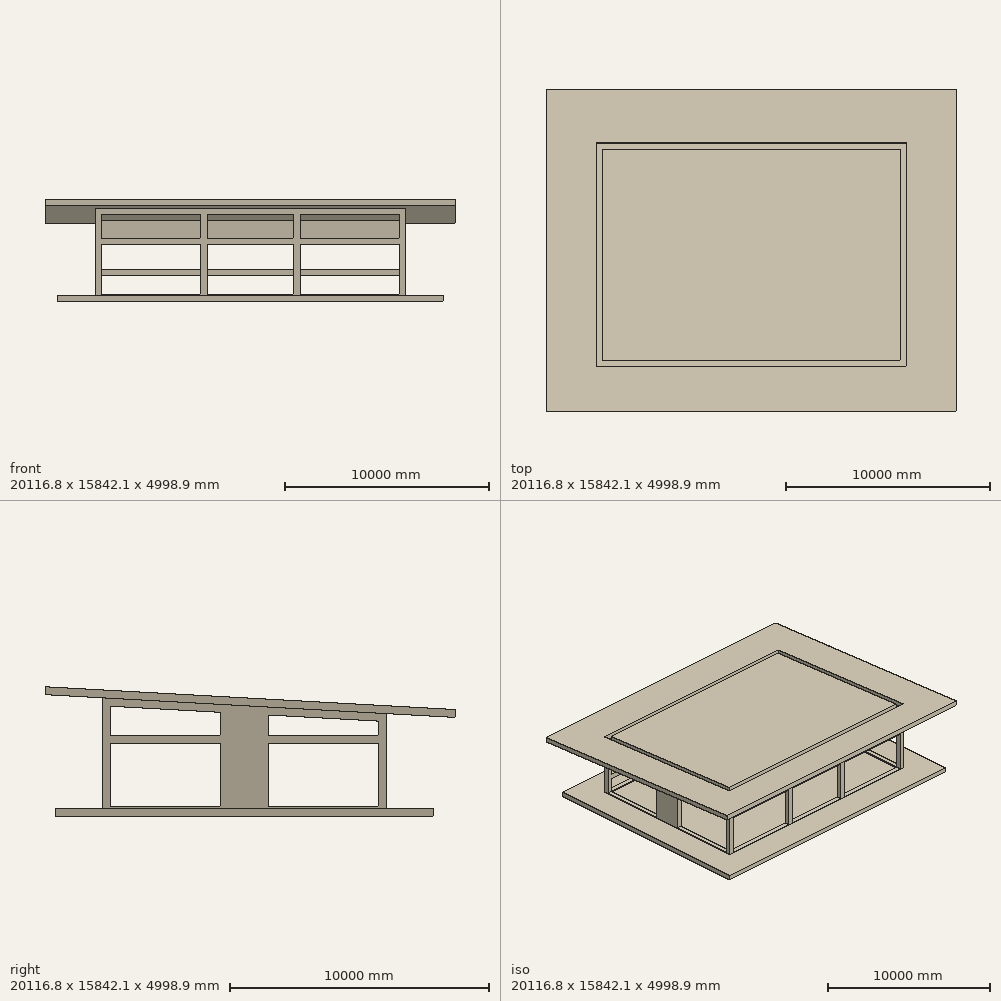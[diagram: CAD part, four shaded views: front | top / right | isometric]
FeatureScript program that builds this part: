
annotation { "Feature Type Name" : "Feature", "Feature Type Description" : "" }
export const myFeature = defineFeature(function(context is Context, id is Id, definition is map)
    precondition{}
    {
        {
            var Q0;
            Q0=qCreatedBy(makeId("Top.planeOp"),FACE);
            var sketch = newSketch(context, id + "F0", { "sketchPlane" : qUnion([Q0])});
            skLineSegment(sketch, "E0.bottom", {"start": v(9448.8, 7315.2) * mm, "end": v(-9448.8, 7315.2) * mm});
            skLineSegment(sketch, "E0.top", {"start": v(9448.8, -7315.2) * mm, "end": v(-9448.8, -7315.2) * mm});
            skLineSegment(sketch, "E0.left", {"start": v(9448.8, 7315.2) * mm, "end": v(9448.8, -7315.2) * mm});
            skLineSegment(sketch, "E0.right", {"start": v(-9448.8, 7315.2) * mm, "end": v(-9448.8, -7315.2) * mm});
            skPoint(sketch, "E0.middle", {"position": v(0, 0) * mm});
            skSolve(sketch);
        }
        {
            var Q0;
            Q0=makeQuery(id+"F0.imprint","IMPRINT",FACE,{"disambiguationData":[TD([[makeQuery(id+"F0.imprint","IMPRINT",EDGE,{"derivedFrom":sQuery(id+"F0.wireOp",EDGE,"E0.bottom")}),1.0]])]});
            extrude(context, id + "F1", {"entities" : qUnion([Q0]), "oppositeDirection" : true, "depth" : 304.8 * mm, "offsetDistance" : 30.48 * mm});
        }
        {
            var Q0;
            Q0=makeQuery(id+"F1.opExtrude","CAP_FACE",FACE,{"disambiguationData":[OSD([sQuery(id+"F0.wireOp",EDGE,"E0.bottom"),sQuery(id+"F0.wireOp",EDGE,"E0.top"),sQuery(id+"F0.wireOp",EDGE,"E0.left"),sQuery(id+"F0.wireOp",EDGE,"E0.right")])],"isStart":true});
            var sketch = newSketch(context, id + "F2", { "sketchPlane" : qUnion([Q0])});
            skLineSegment(sketch, "E1.bottom", {"start": v(7620, 5486.4) * mm, "end": v(-7620, 5486.4) * mm});
            skLineSegment(sketch, "E1.top", {"start": v(7620, -5486.4) * mm, "end": v(-7620, -5486.4) * mm});
            skLineSegment(sketch, "E1.left", {"start": v(7620, 5486.4) * mm, "end": v(7620, -5486.4) * mm});
            skLineSegment(sketch, "E1.right", {"start": v(-7620, 5486.4) * mm, "end": v(-7620, -5486.4) * mm});
            skPoint(sketch, "E1.middle", {"position": v(0, 0) * mm});
            skSolve(sketch);
        }
        {
            var Q0;
            Q0=makeQuery(id+"F2.imprint","IMPRINT",FACE,{"disambiguationData":[TD([[makeQuery(id+"F2.imprint","IMPRINT",EDGE,{"derivedFrom":sQuery(id+"F2.wireOp",EDGE,"E1.bottom")}),1.0]])]});
            extrude(context, id + "F3", {"entities" : qUnion([Q0]), "depth" : 4267.2 * mm, "offsetDistance" : 30.48 * mm});
        }
        {
            var Q0;
            Q0=makeQuery(id+"F3.opExtrude","SWEPT_FACE",FACE,{"disambiguationData":[OSD([sQuery(id+"F2.wireOp",EDGE,"E1.right")])]});
            var sketch = newSketch(context, id + "F4", { "sketchPlane" : qUnion([Q0])});
            skLineSegment(sketch, "E2", {"start": v(-5486.4, 3657.6) * mm, "end": v(5486.4, 4267.2) * mm});
            skSolve(sketch);
        }
        {
            var Q0;
            {var subQ0=sQuery(id+"F4.wireOp",EDGE,"E2");Q0=makeQuery(id+"F4.imprint","IMPRINT",FACE,{"disambiguationData":[TD([[makeQuery(id+"F4.imprint","IMPRINT",EDGE,{"derivedFrom":subQ0}),1.0]])]});}
            var Q1;
            Q1=makeQuery(id+"F3.opExtrude","SWEPT_FACE",FACE,{"disambiguationData":[OSD([sQuery(id+"F2.wireOp",EDGE,"E1.left")])]});
            extrude(context, id + "F5", {"entities" : qUnion([Q0]), "operationType" : NewBodyOperationType.REMOVE, "endBound" : BoundingType.UP_TO_SURFACE, "oppositeDirection" : true, "depth" : 10928.62 * mm, "endBoundEntityFace" : qUnion([Q1]), "offsetDistance" : 30.48 * mm});
        }
        {
            var Q0;
            Q0=makeQuery(id+"F5.boolean.opBoolean","COPY",FACE,{"derivedFrom":makeQuery(id+"F5.opExtrude","SWEPT_FACE",FACE,{"disambiguationData":[OSD([sQuery(id+"F4.wireOp",EDGE,"E2")])]})});
            var Q1;
            Q1=makeQuery(id+"F3.opExtrude","CAP_FACE",FACE,{"disambiguationData":[OSD([sQuery(id+"F2.wireOp",EDGE,"E1.bottom"),sQuery(id+"F2.wireOp",EDGE,"E1.top"),sQuery(id+"F2.wireOp",EDGE,"E1.left"),sQuery(id+"F2.wireOp",EDGE,"E1.right")])],"isStart":true});
            shell(context, id + "F6", {"entities" : qUnion([Q0, Q1]), "thickness" : 304.8 * mm});
        }
        {
            var Q0;
            Q0=makeQuery(id+"F5.boolean.opBoolean","COPY",FACE,{"derivedFrom":makeQuery(id+"F5.opExtrude","SWEPT_FACE",FACE,{"disambiguationData":[OSD([sQuery(id+"F4.wireOp",EDGE,"E2")])]})});
            var sketch = newSketch(context, id + "F7", { "sketchPlane" : qUnion([Q0])});
            skLineSegment(sketch, "E3.bottom", {"start": v(-10058.4, -7924.8) * mm, "end": v(10058.4, -7924.8) * mm});
            skLineSegment(sketch, "E3.top", {"start": v(-10058.4, 7924.8) * mm, "end": v(10058.4, 7924.8) * mm});
            skLineSegment(sketch, "E3.left", {"start": v(-10058.4, -7924.8) * mm, "end": v(-10058.4, 7924.8) * mm});
            skLineSegment(sketch, "E3.right", {"start": v(10058.4, -7924.8) * mm, "end": v(10058.4, 7924.8) * mm});
            skPoint(sketch, "E3.middle", {"position": v(0, 0) * mm});
            skSolve(sketch);
        }
        {
            var Q0;
            Q0=makeQuery(id+"F7.imprint","IMPRINT",FACE,{"disambiguationData":[TD([[makeQuery(id+"F7.imprint","IMPRINT",EDGE,{"derivedFrom":sQuery(id+"F7.wireOp",EDGE,"E3.bottom")}),1.0]])]});
            var Q1;
            {var subQ0=sQuery(id+"F4.wireOp",EDGE,"E2");Q1=makeQuery(id+"F7.imprint","IMPRINT",FACE,{"disambiguationData":[TD([[makeQuery(id+"F7.imprint","IMPRINT",EDGE,{"derivedFrom":makeQuery(id+"F6.opShell","OFFSET_EDGE",EDGE,{"disambiguationData":[OSD([subQ0])]})}),1.0]])]});}
            var Q2;
            {var subQ0=sQuery(id+"F4.wireOp",EDGE,"E2");Q2=makeQuery(id+"F7.imprint","IMPRINT",FACE,{"disambiguationData":[TD([[makeQuery(id+"F7.imprint","IMPRINT",EDGE,{"derivedFrom":makeQuery(id+"F5.boolean.opBoolean","COPY",EDGE,{"derivedFrom":makeQuery(id+"F5.opExtrude","CAP_EDGE",EDGE,{"disambiguationData":[OSD([subQ0])],"isStart":true})})}),1.0]])]});}
            extrude(context, id + "F8", {"entities" : qUnion([Q0, Q1, Q2]), "depth" : 304.8 * mm, "offsetDistance" : 30.48 * mm});
        }
        {
            var Q0;
            Q0=makeQuery(id+"F3.opExtrude","SWEPT_FACE",FACE,{"disambiguationData":[OSD([sQuery(id+"F2.wireOp",EDGE,"E1.top")])]});
            var sketch = newSketch(context, id + "F9", { "sketchPlane" : qUnion([Q0])});
            skLineSegment(sketch, "E4.bottom", {"start": v(-7315.2, 50.8) * mm, "end": v(-2438.4, 50.8) * mm});
            skLineSegment(sketch, "E4.top", {"start": v(-7315.2, 2489.2) * mm, "end": v(-2438.4, 2489.2) * mm});
            skLineSegment(sketch, "E4.left", {"start": v(-7315.2, 50.8) * mm, "end": v(-7315.2, 2489.2) * mm});
            skLineSegment(sketch, "E4.right", {"start": v(-2438.4, 50.8) * mm, "end": v(-2438.4, 2489.2) * mm});
            skLineSegment(sketch, "E5.bottom", {"start": v(-2133.6, 2489.2) * mm, "end": v(2133.6, 2489.2) * mm});
            skLineSegment(sketch, "E5.top", {"start": v(-2133.6, 50.8) * mm, "end": v(2133.6, 50.8) * mm});
            skLineSegment(sketch, "E5.left", {"start": v(-2133.6, 2489.2) * mm, "end": v(-2133.6, 50.8) * mm});
            skLineSegment(sketch, "E5.right", {"start": v(2133.6, 2489.2) * mm, "end": v(2133.6, 50.8) * mm});
            skLineSegment(sketch, "E6.bottom", {"start": v(2438.4, 2489.2) * mm, "end": v(7315.2, 2489.2) * mm});
            skLineSegment(sketch, "E6.top", {"start": v(2438.4, 50.8) * mm, "end": v(7315.2, 50.8) * mm});
            skLineSegment(sketch, "E6.left", {"start": v(2438.4, 2489.2) * mm, "end": v(2438.4, 50.8) * mm});
            skLineSegment(sketch, "E6.right", {"start": v(7315.2, 2489.2) * mm, "end": v(7315.2, 50.8) * mm});
            skSolve(sketch);
        }
        {
            var Q0;
            Q0=makeQuery(id+"F9.imprint","IMPRINT",FACE,{"disambiguationData":[TD([[makeQuery(id+"F9.imprint","IMPRINT",EDGE,{"derivedFrom":sQuery(id+"F9.wireOp",EDGE,"E5.bottom")}),-1.0]])]});
            var Q1;
            Q1=makeQuery(id+"F9.imprint","IMPRINT",FACE,{"disambiguationData":[TD([[makeQuery(id+"F9.imprint","IMPRINT",EDGE,{"derivedFrom":sQuery(id+"F9.wireOp",EDGE,"E6.bottom")}),-1.0]])]});
            var Q2;
            Q2=makeQuery(id+"F9.imprint","IMPRINT",FACE,{"disambiguationData":[TD([[makeQuery(id+"F9.imprint","IMPRINT",EDGE,{"derivedFrom":sQuery(id+"F9.wireOp",EDGE,"E4.bottom")}),1.0]])]});
            var Q3;
            Q3=makeQuery(id+"F3.opExtrude","SWEPT_FACE",FACE,{"disambiguationData":[OSD([sQuery(id+"F2.wireOp",EDGE,"E1.bottom")])]});
            extrude(context, id + "F10", {"entities" : qUnion([Q0, Q1, Q2]), "operationType" : NewBodyOperationType.REMOVE, "endBound" : BoundingType.UP_TO_SURFACE, "oppositeDirection" : true, "depth" : 1883.04 * mm, "endBoundEntityFace" : qUnion([Q3]), "offsetDistance" : 30.48 * mm});
        }
        {
            var Q0;
            Q0=makeQuery(id+"F3.opExtrude","SWEPT_FACE",FACE,{"disambiguationData":[OSD([sQuery(id+"F2.wireOp",EDGE,"E1.right")])]});
            var sketch = newSketch(context, id + "F11", { "sketchPlane" : qUnion([Q0])});
            skLineSegment(sketch, "E7.bottom", {"start": v(-5181.6, 2489.2) * mm, "end": v(-914.4, 2489.2) * mm});
            skLineSegment(sketch, "E7.top", {"start": v(-5181.6, 50.8) * mm, "end": v(-914.4, 50.8) * mm});
            skLineSegment(sketch, "E7.left", {"start": v(-5181.6, 2489.2) * mm, "end": v(-5181.6, 50.8) * mm});
            skLineSegment(sketch, "E7.right", {"start": v(-914.4, 2489.2) * mm, "end": v(-914.4, 50.8) * mm});
            skLineSegment(sketch, "E8.bottom", {"start": v(914.4, 2489.2) * mm, "end": v(5181.6, 2489.2) * mm});
            skLineSegment(sketch, "E8.top", {"start": v(914.4, 50.8) * mm, "end": v(5181.6, 50.8) * mm});
            skLineSegment(sketch, "E8.left", {"start": v(914.4, 2489.2) * mm, "end": v(914.4, 50.8) * mm});
            skLineSegment(sketch, "E8.right", {"start": v(5181.6, 2489.2) * mm, "end": v(5181.6, 50.8) * mm});
            skSolve(sketch);
        }
        {
            var Q0;
            Q0=makeQuery(id+"F11.imprint","IMPRINT",FACE,{"disambiguationData":[TD([[makeQuery(id+"F11.imprint","IMPRINT",EDGE,{"derivedFrom":sQuery(id+"F11.wireOp",EDGE,"E7.bottom")}),-1.0]])]});
            var Q1;
            Q1=makeQuery(id+"F11.imprint","IMPRINT",FACE,{"disambiguationData":[TD([[makeQuery(id+"F11.imprint","IMPRINT",EDGE,{"derivedFrom":sQuery(id+"F11.wireOp",EDGE,"E8.bottom")}),-1.0]])]});
            var Q2;
            Q2=makeQuery(id+"F3.opExtrude","SWEPT_FACE",FACE,{"disambiguationData":[OSD([sQuery(id+"F2.wireOp",EDGE,"E1.left")])]});
            extrude(context, id + "F12", {"entities" : qUnion([Q0, Q1]), "operationType" : NewBodyOperationType.REMOVE, "endBound" : BoundingType.UP_TO_SURFACE, "oppositeDirection" : true, "depth" : 30.48 * mm, "endBoundEntityFace" : qUnion([Q2]), "offsetDistance" : 30.48 * mm});
        }
        {
            var Q0;
            Q0=makeQuery(id+"F3.opExtrude","SWEPT_FACE",FACE,{"disambiguationData":[OSD([sQuery(id+"F2.wireOp",EDGE,"E1.top")])]});
            var sketch = newSketch(context, id + "F13", { "sketchPlane" : qUnion([Q0])});
            skLineSegment(sketch, "E9.bottom", {"start": v(-7315.2, 2794) * mm, "end": v(-2438.4, 2794) * mm});
            skLineSegment(sketch, "E9.top", {"start": v(-7315.2, 3962.4) * mm, "end": v(-2438.4, 3962.4) * mm});
            skLineSegment(sketch, "E9.left", {"start": v(-7315.2, 2794) * mm, "end": v(-7315.2, 3962.4) * mm});
            skLineSegment(sketch, "E9.right", {"start": v(-2438.4, 2794) * mm, "end": v(-2438.4, 3962.4) * mm});
            skLineSegment(sketch, "E10.bottom", {"start": v(-2133.6, 3962.4) * mm, "end": v(2133.6, 3962.4) * mm});
            skLineSegment(sketch, "E10.top", {"start": v(-2133.6, 2794) * mm, "end": v(2133.6, 2794) * mm});
            skLineSegment(sketch, "E10.left", {"start": v(-2133.6, 3962.4) * mm, "end": v(-2133.6, 2794) * mm});
            skLineSegment(sketch, "E10.right", {"start": v(2133.6, 3962.4) * mm, "end": v(2133.6, 2794) * mm});
            skLineSegment(sketch, "E11.bottom", {"start": v(2438.4, 3962.4) * mm, "end": v(7315.2, 3962.4) * mm});
            skLineSegment(sketch, "E11.top", {"start": v(2438.4, 2794) * mm, "end": v(7315.2, 2794) * mm});
            skLineSegment(sketch, "E11.left", {"start": v(2438.4, 3962.4) * mm, "end": v(2438.4, 2794) * mm});
            skLineSegment(sketch, "E11.right", {"start": v(7315.2, 3962.4) * mm, "end": v(7315.2, 2794) * mm});
            skSolve(sketch);
        }
        {
            var Q0;
            Q0=makeQuery(id+"F13.imprint","IMPRINT",FACE,{"disambiguationData":[TD([[makeQuery(id+"F13.imprint","IMPRINT",EDGE,{"derivedFrom":sQuery(id+"F13.wireOp",EDGE,"E11.bottom")}),-1.0]])]});
            var Q1;
            Q1=makeQuery(id+"F13.imprint","IMPRINT",FACE,{"disambiguationData":[TD([[makeQuery(id+"F13.imprint","IMPRINT",EDGE,{"derivedFrom":sQuery(id+"F13.wireOp",EDGE,"E10.bottom")}),-1.0]])]});
            var Q2;
            Q2=makeQuery(id+"F13.imprint","IMPRINT",FACE,{"disambiguationData":[TD([[makeQuery(id+"F13.imprint","IMPRINT",EDGE,{"derivedFrom":sQuery(id+"F13.wireOp",EDGE,"E9.bottom")}),1.0]])]});
            var Q3;
            Q3=makeQuery(id+"F6.opShell","OFFSET_FACE",FACE,{"disambiguationData":[OSD([sQuery(id+"F2.wireOp",EDGE,"E1.top")])]});
            extrude(context, id + "F14", {"entities" : qUnion([Q0, Q1, Q2]), "operationType" : NewBodyOperationType.REMOVE, "endBound" : BoundingType.UP_TO_NEXT, "oppositeDirection" : true, "depth" : 1625.5 * mm, "endBoundEntityFace" : qUnion([Q3]), "offsetDistance" : 30.48 * mm});
        }
        {
            var Q0;
            Q0=makeQuery(id+"F3.opExtrude","SWEPT_FACE",FACE,{"disambiguationData":[OSD([sQuery(id+"F2.wireOp",EDGE,"E1.right")])]});
            var sketch = newSketch(context, id + "F15", { "sketchPlane" : qUnion([Q0])});
            skLineSegment(sketch, "E12", {"start": v(5181.6, 2794) * mm, "end": v(5181.6, 3945) * mm});
            skLineSegment(sketch, "E13", {"start": v(5181.6, 3945) * mm, "end": v(914.4, 3707.93) * mm});
            skLineSegment(sketch, "E14", {"start": v(914.4, 3707.93) * mm, "end": v(914.4, 2794) * mm});
            skLineSegment(sketch, "E15", {"start": v(914.4, 2794) * mm, "end": v(5181.6, 2794) * mm});
            skPoint(sketch, "E16.orphan", {"position": v(5181.6, 2794) * mm});
            skLineSegment(sketch, "E17", {"start": v(-914.4, 2794) * mm, "end": v(-914.4, 3606.33) * mm});
            skLineSegment(sketch, "E18", {"start": v(-914.4, 3606.33) * mm, "end": v(-5181.6, 3369.26) * mm});
            skLineSegment(sketch, "E19", {"start": v(-914.4, 2794) * mm, "end": v(-5181.6, 2794) * mm});
            skLineSegment(sketch, "E20", {"start": v(-5181.6, 3369.26) * mm, "end": v(-5181.6, 2794) * mm});
            skSolve(sketch);
        }
        {
            var Q0;
            Q0=makeQuery(id+"F15.imprint","IMPRINT",FACE,{"disambiguationData":[TD([[makeQuery(id+"F15.imprint","IMPRINT",EDGE,{"derivedFrom":sQuery(id+"F15.wireOp",EDGE,"E17")}),1.0]])]});
            var Q1;
            Q1=makeQuery(id+"F15.imprint","IMPRINT",FACE,{"disambiguationData":[TD([[makeQuery(id+"F15.imprint","IMPRINT",EDGE,{"derivedFrom":sQuery(id+"F15.wireOp",EDGE,"E12")}),1.0]])]});
            var Q2;
            Q2=makeQuery(id+"F3.opExtrude","SWEPT_FACE",FACE,{"disambiguationData":[OSD([sQuery(id+"F2.wireOp",EDGE,"E1.left")])]});
            extrude(context, id + "F16", {"entities" : qUnion([Q0, Q1]), "operationType" : NewBodyOperationType.REMOVE, "endBound" : BoundingType.UP_TO_SURFACE, "oppositeDirection" : true, "depth" : 30.48 * mm, "endBoundEntityFace" : qUnion([Q2]), "offsetDistance" : 30.48 * mm});
        }
        {
            var Q0;
            {var subQ0=sQuery(id+"F2.wireOp",EDGE,"E1.bottom");Q0=makeQuery(id+"F10.boolean.opBoolean","COPY",FACE,{"disambiguationData":[TD([makeQuery(id+"F3.opExtrude","SWEPT_FACE",FACE,{"disambiguationData":[OSD([subQ0])]})])],"derivedFrom":makeQuery(id+"F10.opExtrude","SWEPT_FACE",FACE,{"disambiguationData":[OSD([sQuery(id+"F9.wireOp",EDGE,"E5.top")])]})});}
            cPlane(context, id + "F17", {"entities" : qUnion([Q0]), "cplaneType" : CPlaneType.OFFSET, "offset" : 914.4 * mm, "width" : 152.4 * mm, "height" : 152.4 * mm});
        }
        {
            var Q0;
            Q0=qCreatedBy(id+"F17.planeOp",FACE);
            var sketch = newSketch(context, id + "F18", { "sketchPlane" : qUnion([Q0])});
            skLineSegment(sketch, "E21.0.0", {"start": v(-7315.2, 5181.6) * mm, "end": v(-2438.4, 5181.6) * mm});
            skLineSegment(sketch, "E21.0.1", {"start": v(-2438.4, 5181.6) * mm, "end": v(-2438.4, 5486.4) * mm});
            skLineSegment(sketch, "E21.0.2", {"start": v(-2438.4, 5486.4) * mm, "end": v(-7315.2, 5486.4) * mm});
            skLineSegment(sketch, "E21.0.3", {"start": v(-7315.2, 5486.4) * mm, "end": v(-7315.2, 5181.6) * mm});
            skLineSegment(sketch, "E22.0.0", {"start": v(-2133.6, 5181.6) * mm, "end": v(2133.6, 5181.6) * mm});
            skLineSegment(sketch, "E22.0.1", {"start": v(2133.6, 5181.6) * mm, "end": v(2133.6, 5486.4) * mm});
            skLineSegment(sketch, "E22.0.2", {"start": v(2133.6, 5486.4) * mm, "end": v(-2133.6, 5486.4) * mm});
            skLineSegment(sketch, "E22.0.3", {"start": v(-2133.6, 5486.4) * mm, "end": v(-2133.6, 5181.6) * mm});
            skLineSegment(sketch, "E23.0.0", {"start": v(2438.4, 5181.6) * mm, "end": v(7315.2, 5181.6) * mm});
            skLineSegment(sketch, "E23.0.1", {"start": v(7315.2, 5181.6) * mm, "end": v(7315.2, 5486.4) * mm});
            skLineSegment(sketch, "E23.0.2", {"start": v(7315.2, 5486.4) * mm, "end": v(2438.4, 5486.4) * mm});
            skLineSegment(sketch, "E23.0.3", {"start": v(2438.4, 5486.4) * mm, "end": v(2438.4, 5181.6) * mm});
            skSolve(sketch);
        }
        {
            var Q0;
            Q0=makeQuery(id+"F18.imprint","IMPRINT",FACE,{"disambiguationData":[TD([[makeQuery(id+"F18.imprint","IMPRINT",EDGE,{"derivedFrom":sQuery(id+"F18.wireOp",EDGE,"E23.0.0")}),1.0]])]});
            var Q1;
            Q1=makeQuery(id+"F18.imprint","IMPRINT",FACE,{"disambiguationData":[TD([[makeQuery(id+"F18.imprint","IMPRINT",EDGE,{"derivedFrom":sQuery(id+"F18.wireOp",EDGE,"E22.0.0")}),1.0]])]});
            var Q2;
            Q2=makeQuery(id+"F18.imprint","IMPRINT",FACE,{"disambiguationData":[TD([[makeQuery(id+"F18.imprint","IMPRINT",EDGE,{"derivedFrom":sQuery(id+"F18.wireOp",EDGE,"E21.0.0")}),1.0]])]});
            extrude(context, id + "F19", {"entities" : qUnion([Q0, Q1, Q2]), "operationType" : NewBodyOperationType.ADD, "depth" : 304.8 * mm, "offsetDistance" : 30.48 * mm});
        }
    });
